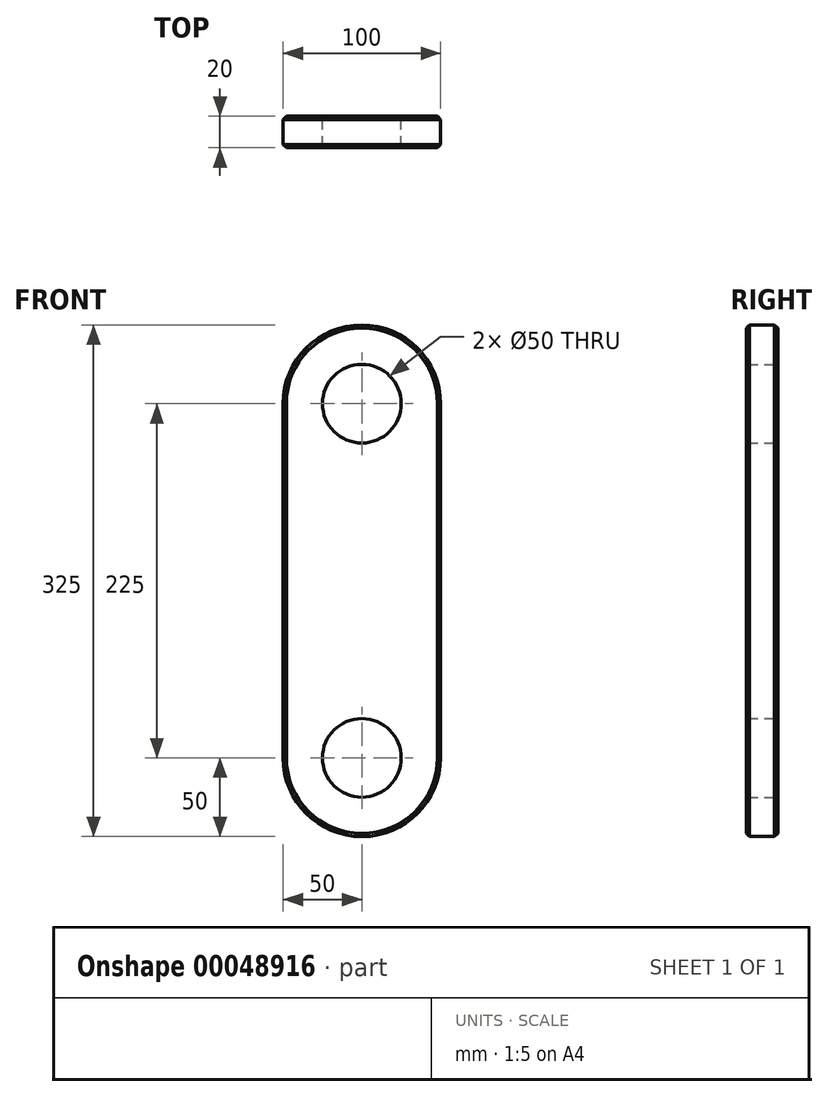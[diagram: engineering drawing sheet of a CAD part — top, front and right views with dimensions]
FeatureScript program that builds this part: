
annotation { "Feature Type Name" : "Feature", "Feature Type Description" : "" }
export const myFeature = defineFeature(function(context is Context, id is Id, definition is map)
    precondition{}
    {
        {
            var Q0;
            Q0=qCreatedBy(makeId("Front.planeOp"),FACE);
            var sketch = newSketch(context, id + "F0", { "sketchPlane" : qUnion([Q0])});
            skCircle(sketch, "E0", {"center": v(0, 0) * mm, "radius": 25 * mm});
            skLineSegment(sketch, "E1", {"start": v(0, 0) * mm, "end": v(0, 225) * mm, "construction": true});
            skCircle(sketch, "E2", {"center": v(0, 225) * mm, "radius": 25 * mm});
            skCircle(sketch, "E3", {"center": v(0, 225) * mm, "radius": 50 * mm});
            skCircle(sketch, "E4", {"center": v(0, 0) * mm, "radius": 50 * mm});
            skLineSegment(sketch, "E5", {"start": v(0, 225) * mm, "end": v(-50, 225) * mm, "construction": true});
            skLineSegment(sketch, "E6", {"start": v(0, 225) * mm, "end": v(50, 225) * mm, "construction": true});
            skLineSegment(sketch, "E7", {"start": v(0, 0) * mm, "end": v(-50, 0) * mm, "construction": true});
            skLineSegment(sketch, "E8", {"start": v(0, 0) * mm, "end": v(50, 0) * mm, "construction": true});
            skLineSegment(sketch, "E9", {"start": v(-50, 225) * mm, "end": v(-50, 0) * mm});
            skLineSegment(sketch, "E10", {"start": v(50, 225) * mm, "end": v(50, 0) * mm});
            skSolve(sketch);
        }
        {
            var Q0;
            Q0=makeQuery(id+"F0.imprint","IMPRINT",FACE,{"disambiguationData":[TD([[makeQuery(id+"F0.imprint","IMPRINT",EDGE,{"derivedFrom":sQuery(id+"F0.wireOp",EDGE,"E2")}),-1.0]])]});
            var Q1;
            {var subQ1=sQuery(id+"F0.wireOp",EDGE,"E9");Q1=makeQuery(id+"F0.imprint","IMPRINT",FACE,{"disambiguationData":[TD([[makeQuery(id+"F0.imprint","IMPRINT",EDGE,{"derivedFrom":subQ1}),1.0]])]});}
            var Q2;
            Q2=makeQuery(id+"F0.imprint","IMPRINT",FACE,{"disambiguationData":[TD([[makeQuery(id+"F0.imprint","IMPRINT",EDGE,{"derivedFrom":sQuery(id+"F0.wireOp",EDGE,"E0")}),-1.0]])]});
            extrude(context, id + "F1", {"entities" : qUnion([Q0, Q1, Q2]), "depth" : 20 * mm});
        }
        {
            var Q0;
            Q0=makeQuery(id+"F1.opExtrude","CAP_EDGE",EDGE,{"disambiguationData":[OSD([sQuery(id+"F0.wireOp",EDGE,"E3")])],"isStart":false});
            var Q1;
            Q1=makeQuery(id+"F1.opExtrude","CAP_EDGE",EDGE,{"disambiguationData":[OSD([sQuery(id+"F0.wireOp",EDGE,"E3")])],"isStart":true});
            chamfer(context, id + "F2", {"entities" : qUnion([Q0, Q1]), "chamferType" : ChamferType.OFFSET_ANGLE, "width" : 2 * mm, "oppositeDirection" : false, "angle" : 45 * degree, "tangentPropagation" : true});
        }
    });
